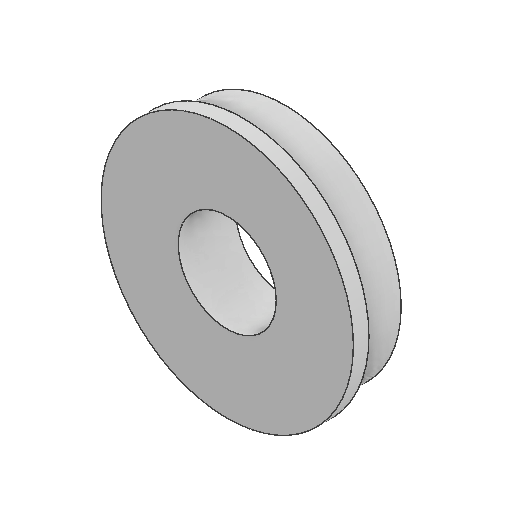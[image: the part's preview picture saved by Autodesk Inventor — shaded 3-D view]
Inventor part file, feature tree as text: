
AUTODESK INVENTOR PART (.ipt)
format: ipt  version: 2025.2 (Build 292293000, 293)  size: 112,640 bytes
history: native  units: in
note: dims shown in document units (in); Inventor stores cm internally (conversion verified against a paired STEP export)
features: extrude x2, sketch x2
ambient origin geometry x8: Origin, YZ Plane, XZ Plane, XY Plane, X Axis, Y Axis, Z Axis, Center Point
bodies: Solid1 (feature_tree)
feature tree (4):
  extrude  "Extrusion1"  Depth=0.315in
  extrude  "Extrusion2"  Depth=0.05in TaperAngle=0.0deg
  sketch  "Sketch1"  dims[d0=0.748in d1=0.315in]
  sketch  "Sketch2"  dims[d2=0.135in d3=0.0in d4=0.05in d5=0.0in]
